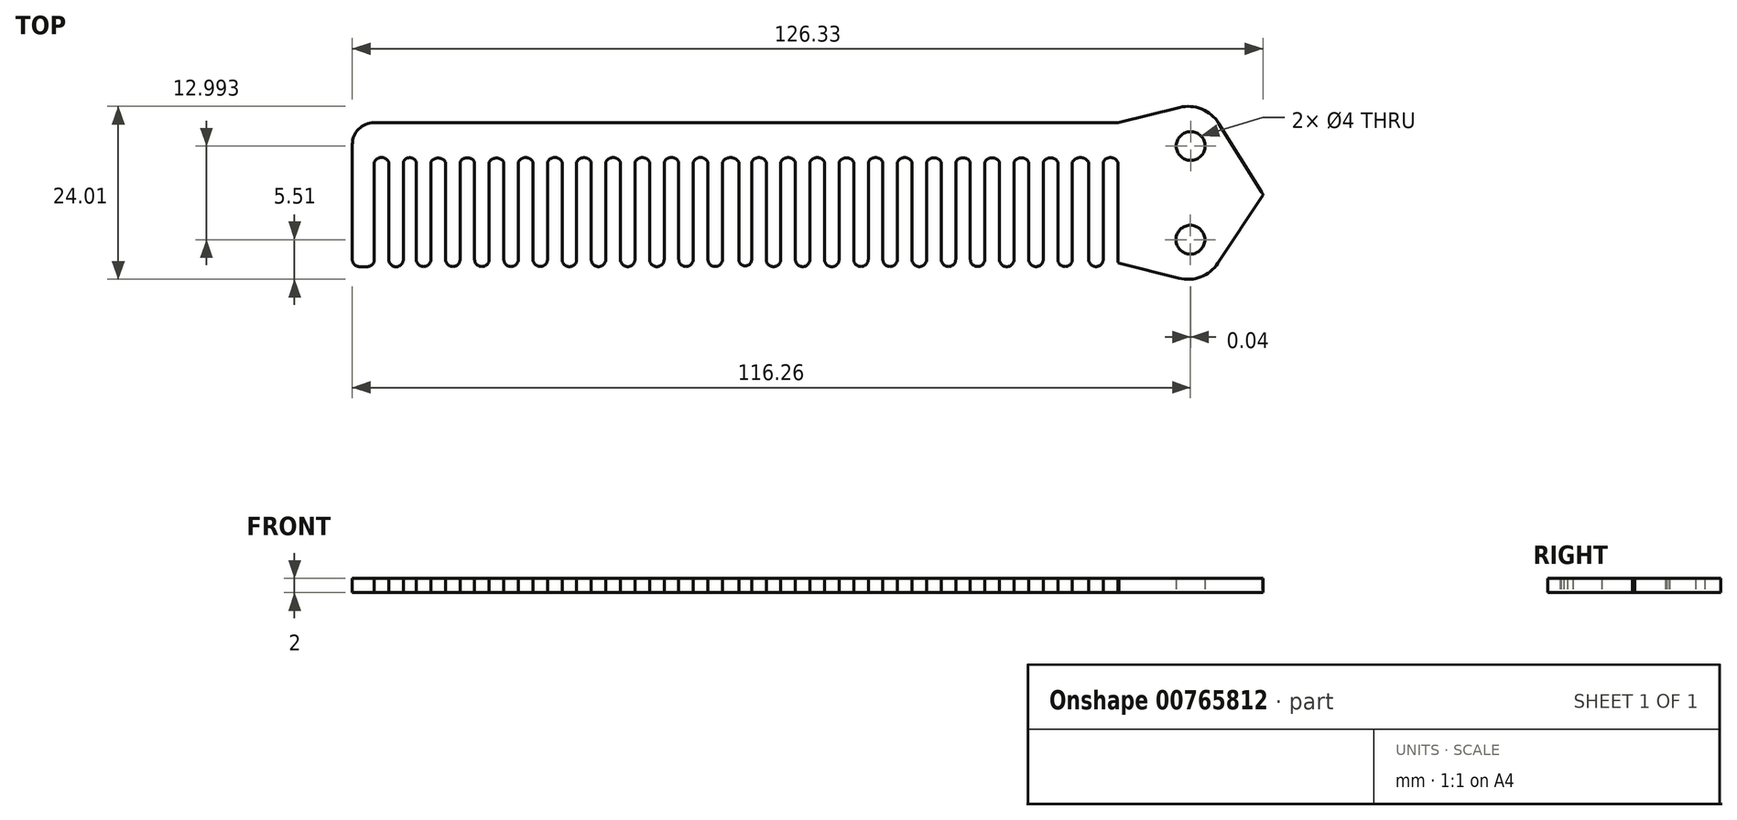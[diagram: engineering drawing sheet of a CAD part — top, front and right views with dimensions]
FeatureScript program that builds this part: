
annotation { "Feature Type Name" : "Feature", "Feature Type Description" : "" }
export const myFeature = defineFeature(function(context is Context, id is Id, definition is map)
    precondition{}
    {
        {
            var Q0;
            Q0=qCreatedBy(makeId("Top.planeOp"),FACE);
            var sketch = newSketch(context, id + "F0", { "sketchPlane" : qUnion([Q0])});
            skLineSegment(sketch, "E0.top", {"start": v(-46.52, -4.05) * mm, "end": v(-45.49, -4.05) * mm});
            skLineSegment(sketch, "E1", {"start": v(56.63, 10.5) * mm, "end": v(56.63, -3.03) * mm});
            skLineSegment(sketch, "E2", {"start": v(-44.48, 10.5) * mm, "end": v(-44.48, -3.03) * mm});
            skLineSegment(sketch, "E3", {"start": v(-47.53, 12.92) * mm, "end": v(-47.53, -3.03) * mm});
            skArc(sketch, "E4.filletArc", {"start": v(-44.5, 15.95) * mm, "mid": v(-46.64, 15.07) * mm, "end": v(-47.53, 12.92) * mm});
            skArc(sketch, "E5.filletArc", {"start": v(-47.53, -3.03) * mm, "mid": v(-47.24, -3.75) * mm, "end": v(-46.52, -4.05) * mm});
            skLineSegment(sketch, "E6", {"start": v(-42.48, 10.5) * mm, "end": v(-42.48, -3.04) * mm});
            skLineSegment(sketch, "E7", {"start": v(-40.45, 2.37) * mm, "end": v(-40.45, 10.5) * mm});
            skLineSegment(sketch, "E8", {"start": v(-40.45, 10.5) * mm, "end": v(-40.45, -3.04) * mm});
            skLineSegment(sketch, "E9", {"start": v(-38.66, 2.37) * mm, "end": v(-38.66, 10.5) * mm});
            skLineSegment(sketch, "E10", {"start": v(-38.66, 10.5) * mm, "end": v(-38.66, -3.03) * mm});
            skLineSegment(sketch, "E11", {"start": v(-36.63, 2.37) * mm, "end": v(-36.63, 10.5) * mm});
            skLineSegment(sketch, "E12", {"start": v(-36.63, 10.5) * mm, "end": v(-36.63, -3.03) * mm});
            skLineSegment(sketch, "E13", {"start": v(-34.61, 2.37) * mm, "end": v(-34.61, -3.03) * mm});
            skLineSegment(sketch, "E14", {"start": v(-34.61, -3.03) * mm, "end": v(-34.61, 10.5) * mm});
            skLineSegment(sketch, "E15", {"start": v(-32.59, 2.37) * mm, "end": v(-32.59, -3.03) * mm});
            skLineSegment(sketch, "E16", {"start": v(-32.59, -3.03) * mm, "end": v(-32.59, 10.5) * mm});
            skLineSegment(sketch, "E17", {"start": v(-30.57, 2.37) * mm, "end": v(-30.57, -3.03) * mm});
            skLineSegment(sketch, "E18", {"start": v(-30.57, -3.03) * mm, "end": v(-30.57, 10.5) * mm});
            skLineSegment(sketch, "E19", {"start": v(-28.54, 2.37) * mm, "end": v(-28.54, 10.5) * mm});
            skLineSegment(sketch, "E20", {"start": v(-28.54, 10.5) * mm, "end": v(-28.54, -3.03) * mm});
            skLineSegment(sketch, "E21", {"start": v(-26.52, 2.37) * mm, "end": v(-26.52, 10.5) * mm});
            skLineSegment(sketch, "E22", {"start": v(-26.52, 10.5) * mm, "end": v(-26.52, -3.03) * mm});
            skLineSegment(sketch, "E23", {"start": v(-24.5, 2.37) * mm, "end": v(-24.5, 10.5) * mm});
            skLineSegment(sketch, "E24", {"start": v(-24.5, 10.5) * mm, "end": v(-24.5, -3.03) * mm});
            skLineSegment(sketch, "E25", {"start": v(-22.48, 2.37) * mm, "end": v(-22.48, 10.5) * mm});
            skLineSegment(sketch, "E26", {"start": v(-22.48, 10.5) * mm, "end": v(-22.48, -3.03) * mm});
            skLineSegment(sketch, "E27", {"start": v(-20.45, 2.37) * mm, "end": v(-20.45, -3.03) * mm});
            skLineSegment(sketch, "E28", {"start": v(-20.45, -3.03) * mm, "end": v(-20.45, 10.5) * mm});
            skLineSegment(sketch, "E29", {"start": v(-18.43, 2.37) * mm, "end": v(-18.43, 10.5) * mm});
            skLineSegment(sketch, "E30", {"start": v(-18.43, 10.5) * mm, "end": v(-18.43, -3.03) * mm});
            skLineSegment(sketch, "E31", {"start": v(-16.4, 2.37) * mm, "end": v(-16.4, -3.03) * mm});
            skLineSegment(sketch, "E32", {"start": v(-16.4, -3.03) * mm, "end": v(-16.4, 10.5) * mm});
            skLineSegment(sketch, "E33", {"start": v(-14.39, 2.37) * mm, "end": v(-14.39, -3.03) * mm});
            skLineSegment(sketch, "E34", {"start": v(-14.39, -3.03) * mm, "end": v(-14.39, 10.5) * mm});
            skLineSegment(sketch, "E35", {"start": v(-12.36, 2.37) * mm, "end": v(-12.36, 10.5) * mm});
            skLineSegment(sketch, "E36", {"start": v(-12.36, 10.5) * mm, "end": v(-12.36, -3.03) * mm});
            skLineSegment(sketch, "E37", {"start": v(-10.34, 2.37) * mm, "end": v(-10.34, 10.5) * mm});
            skLineSegment(sketch, "E38", {"start": v(-10.34, 10.5) * mm, "end": v(-10.34, -3.03) * mm});
            skLineSegment(sketch, "E39", {"start": v(-8.32, 2.37) * mm, "end": v(-8.32, -3.03) * mm});
            skLineSegment(sketch, "E40", {"start": v(-8.32, -3.03) * mm, "end": v(-8.32, 10.5) * mm});
            skLineSegment(sketch, "E41", {"start": v(-6.3, 2.37) * mm, "end": v(-6.3, 10.5) * mm});
            skLineSegment(sketch, "E42", {"start": v(-6.3, 10.5) * mm, "end": v(-6.3, -3.03) * mm});
            skLineSegment(sketch, "E43", {"start": v(-4.27, 2.37) * mm, "end": v(-4.27, 10.5) * mm});
            skLineSegment(sketch, "E44", {"start": v(-4.27, 10.5) * mm, "end": v(-4.27, -3.03) * mm});
            skLineSegment(sketch, "E45", {"start": v(-2.25, 2.37) * mm, "end": v(-2.25, 10.5) * mm});
            skLineSegment(sketch, "E46", {"start": v(-2.25, 10.5) * mm, "end": v(-2.25, -3.03) * mm});
            skLineSegment(sketch, "E47", {"start": v(-0.23, 2.37) * mm, "end": v(-0.23, -3.03) * mm});
            skLineSegment(sketch, "E48", {"start": v(-0.23, -3.03) * mm, "end": v(-0.23, 10.5) * mm});
            skLineSegment(sketch, "E49", {"start": v(1.8, 2.37) * mm, "end": v(1.8, 10.5) * mm});
            skLineSegment(sketch, "E50", {"start": v(1.8, 10.5) * mm, "end": v(1.8, -3.03) * mm});
            skLineSegment(sketch, "E51", {"start": v(3.82, 2.37) * mm, "end": v(3.82, -3.03) * mm});
            skLineSegment(sketch, "E52", {"start": v(3.82, -3.03) * mm, "end": v(3.82, 10.5) * mm});
            skLineSegment(sketch, "E53", {"start": v(6.08, 2.37) * mm, "end": v(6.08, 10.5) * mm});
            skLineSegment(sketch, "E54", {"start": v(6.08, 10.5) * mm, "end": v(6.08, -3.03) * mm});
            skLineSegment(sketch, "E55", {"start": v(7.86, 2.37) * mm, "end": v(7.86, 10.5) * mm});
            skLineSegment(sketch, "E56", {"start": v(7.86, 10.5) * mm, "end": v(7.86, -3.03) * mm});
            skLineSegment(sketch, "E57", {"start": v(9.89, 2.37) * mm, "end": v(9.89, 10.5) * mm});
            skLineSegment(sketch, "E58", {"start": v(9.89, 10.5) * mm, "end": v(9.89, -3.03) * mm});
            skLineSegment(sketch, "E59", {"start": v(11.9, 2.37) * mm, "end": v(11.9, 10.5) * mm});
            skLineSegment(sketch, "E60", {"start": v(11.9, 10.5) * mm, "end": v(11.9, -3.03) * mm});
            skLineSegment(sketch, "E61", {"start": v(13.93, 2.37) * mm, "end": v(13.93, 10.5) * mm});
            skLineSegment(sketch, "E62", {"start": v(13.93, 10.5) * mm, "end": v(13.93, -3.03) * mm});
            skLineSegment(sketch, "E63", {"start": v(15.95, 2.37) * mm, "end": v(15.95, 10.5) * mm});
            skLineSegment(sketch, "E64", {"start": v(15.95, 10.5) * mm, "end": v(15.95, -3.03) * mm});
            skLineSegment(sketch, "E65", {"start": v(17.98, 10.5) * mm, "end": v(17.98, -3.06) * mm});
            skLineSegment(sketch, "E66", {"start": v(20, 2.37) * mm, "end": v(20, 10.5) * mm});
            skLineSegment(sketch, "E67", {"start": v(20, 10.5) * mm, "end": v(20, -3.06) * mm});
            skLineSegment(sketch, "E68", {"start": v(22.02, 2.37) * mm, "end": v(22.02, 10.5) * mm});
            skLineSegment(sketch, "E69", {"start": v(24.04, 2.37) * mm, "end": v(24.04, 10.5) * mm});
            skLineSegment(sketch, "E70", {"start": v(24.04, 2.37) * mm, "end": v(24.04, -3.03) * mm});
            skLineSegment(sketch, "E71", {"start": v(26.07, 2.37) * mm, "end": v(26.07, 10.5) * mm});
            skLineSegment(sketch, "E72", {"start": v(26.07, 10.5) * mm, "end": v(26.07, -3.03) * mm});
            skLineSegment(sketch, "E73", {"start": v(28.09, 2.37) * mm, "end": v(28.09, 10.5) * mm});
            skLineSegment(sketch, "E74", {"start": v(28.09, 2.37) * mm, "end": v(28.09, -3.03) * mm});
            skLineSegment(sketch, "E75", {"start": v(30.11, 2.37) * mm, "end": v(30.11, 10.5) * mm});
            skLineSegment(sketch, "E76", {"start": v(30.11, 10.5) * mm, "end": v(30.11, -3.03) * mm});
            skLineSegment(sketch, "E77", {"start": v(32.13, 2.37) * mm, "end": v(32.13, 10.5) * mm});
            skLineSegment(sketch, "E78", {"start": v(32.13, 10.5) * mm, "end": v(32.13, -3.03) * mm});
            skLineSegment(sketch, "E79", {"start": v(34.16, 2.37) * mm, "end": v(34.16, 10.5) * mm});
            skLineSegment(sketch, "E80", {"start": v(34.16, 10.5) * mm, "end": v(34.16, -3.03) * mm});
            skLineSegment(sketch, "E81", {"start": v(36.18, 2.37) * mm, "end": v(36.18, 10.5) * mm});
            skLineSegment(sketch, "E82", {"start": v(36.18, 10.5) * mm, "end": v(36.18, -3.03) * mm});
            skLineSegment(sketch, "E83", {"start": v(38.2, 2.37) * mm, "end": v(38.2, 10.5) * mm});
            skLineSegment(sketch, "E84", {"start": v(38.2, 10.5) * mm, "end": v(38.2, -3.03) * mm});
            skLineSegment(sketch, "E85", {"start": v(40.23, 2.37) * mm, "end": v(40.23, 10.5) * mm});
            skLineSegment(sketch, "E86", {"start": v(40.23, 10.5) * mm, "end": v(40.23, -3.03) * mm});
            skLineSegment(sketch, "E87", {"start": v(42.25, 2.37) * mm, "end": v(42.25, 10.5) * mm});
            skLineSegment(sketch, "E88", {"start": v(42.25, 10.5) * mm, "end": v(42.25, -3.03) * mm});
            skLineSegment(sketch, "E89", {"start": v(44.27, 2.37) * mm, "end": v(44.27, 10.5) * mm});
            skLineSegment(sketch, "E90", {"start": v(44.27, 10.5) * mm, "end": v(44.27, -3.03) * mm});
            skLineSegment(sketch, "E91", {"start": v(46.3, 2.37) * mm, "end": v(46.3, 10.5) * mm});
            skLineSegment(sketch, "E92", {"start": v(46.3, 10.5) * mm, "end": v(46.3, -3.03) * mm});
            skLineSegment(sketch, "E93", {"start": v(48.32, 2.37) * mm, "end": v(48.32, 10.5) * mm});
            skLineSegment(sketch, "E94", {"start": v(48.32, 10.5) * mm, "end": v(48.32, -3.03) * mm});
            skLineSegment(sketch, "E95", {"start": v(50.34, 2.37) * mm, "end": v(50.34, 10.5) * mm});
            skLineSegment(sketch, "E96", {"start": v(50.34, 10.5) * mm, "end": v(50.34, -3.03) * mm});
            skLineSegment(sketch, "E97", {"start": v(52.36, 2.37) * mm, "end": v(52.36, 10.5) * mm});
            skLineSegment(sketch, "E98", {"start": v(52.36, 10.5) * mm, "end": v(52.36, -3.03) * mm});
            skLineSegment(sketch, "E99", {"start": v(54.6, 2.37) * mm, "end": v(54.6, 10.5) * mm});
            skLineSegment(sketch, "E100", {"start": v(54.6, 10.5) * mm, "end": v(54.6, -3.03) * mm});
            skLineSegment(sketch, "E101", {"start": v(58.65, 10.5) * mm, "end": v(58.65, -3.18) * mm});
            skArc(sketch, "E102.filletArc", {"start": v(-45.49, -4.05) * mm, "mid": v(-44.77, -3.75) * mm, "end": v(-44.48, -3.03) * mm});
            skArc(sketch, "E103", {"start": v(-42.48, -3.03) * mm, "mid": v(-41.46, -4.05) * mm, "end": v(-40.45, -3.03) * mm});
            skArc(sketch, "E104", {"start": v(-38.66, -3.03) * mm, "mid": v(-37.65, -4.03) * mm, "end": v(-36.63, -3.03) * mm});
            skArc(sketch, "E105", {"start": v(-34.61, -3.03) * mm, "mid": v(-33.6, -4.03) * mm, "end": v(-32.59, -3.03) * mm});
            skArc(sketch, "E106", {"start": v(-30.57, -3.03) * mm, "mid": v(-29.55, -4.03) * mm, "end": v(-28.54, -3.03) * mm});
            skArc(sketch, "E107", {"start": v(-26.52, -3.03) * mm, "mid": v(-25.5, -4.03) * mm, "end": v(-24.5, -3.03) * mm});
            skArc(sketch, "E108", {"start": v(-22.48, -3.03) * mm, "mid": v(-21.46, -4.02) * mm, "end": v(-20.45, -3.03) * mm});
            skArc(sketch, "E109", {"start": v(-18.43, -3.03) * mm, "mid": v(-17.42, -4.05) * mm, "end": v(-16.4, -3.03) * mm});
            skArc(sketch, "E110", {"start": v(-14.39, -3.03) * mm, "mid": v(-13.37, -4.03) * mm, "end": v(-12.36, -3.03) * mm});
            skArc(sketch, "E111", {"start": v(-10.34, -3.03) * mm, "mid": v(-9.33, -4.03) * mm, "end": v(-8.32, -3.03) * mm});
            skArc(sketch, "E112", {"start": v(-6.3, -3.03) * mm, "mid": v(-5.28, -4.03) * mm, "end": v(-4.27, -3.03) * mm});
            skArc(sketch, "E113", {"start": v(-2.25, -3.03) * mm, "mid": v(-1.24, -4.03) * mm, "end": v(-0.23, -3.03) * mm});
            skArc(sketch, "E114", {"start": v(1.8, -3.03) * mm, "mid": v(2.8, -4.02) * mm, "end": v(3.82, -3.03) * mm});
            skArc(sketch, "E115", {"start": v(9.89, -3.03) * mm, "mid": v(10.9, -4.05) * mm, "end": v(11.9, -3.03) * mm});
            skArc(sketch, "E116", {"start": v(13.93, -3.03) * mm, "mid": v(14.94, -4.05) * mm, "end": v(15.95, -3.03) * mm});
            skArc(sketch, "E117", {"start": v(17.98, -3.03) * mm, "mid": v(18.99, -4.06) * mm, "end": v(20, -3.03) * mm});
            skArc(sketch, "E118", {"start": v(22.02, -3.03) * mm, "mid": v(23.03, -4.03) * mm, "end": v(24.04, -3.03) * mm});
            skArc(sketch, "E119", {"start": v(26.07, -3.03) * mm, "mid": v(27.08, -4.03) * mm, "end": v(28.09, -3.03) * mm});
            skArc(sketch, "E120", {"start": v(30.11, -3.03) * mm, "mid": v(31.12, -4.04) * mm, "end": v(32.13, -3.03) * mm});
            skArc(sketch, "E121", {"start": v(34.16, -3.03) * mm, "mid": v(35.17, -4.03) * mm, "end": v(36.18, -3.03) * mm});
            skArc(sketch, "E122", {"start": v(38.2, -3.03) * mm, "mid": v(39.21, -4.02) * mm, "end": v(40.23, -3.03) * mm});
            skArc(sketch, "E123", {"start": v(42.25, -3.03) * mm, "mid": v(43.26, -4.05) * mm, "end": v(44.27, -3.03) * mm});
            skArc(sketch, "E124", {"start": v(46.3, -3.03) * mm, "mid": v(47.3, -4.04) * mm, "end": v(48.32, -3.03) * mm});
            skArc(sketch, "E125", {"start": v(50.34, -3.03) * mm, "mid": v(51.35, -4.03) * mm, "end": v(52.36, -3.03) * mm});
            skArc(sketch, "E126", {"start": v(54.6, -3.03) * mm, "mid": v(55.62, -4.04) * mm, "end": v(56.63, -3.03) * mm});
            skArc(sketch, "E127.filletArc", {"start": v(58.65, -3.18) * mm, "mid": v(58.7, -3.38) * mm, "end": v(58.81, -3.55) * mm});
            skArc(sketch, "E128", {"start": v(6.08, -3.03) * mm, "mid": v(6.97, -3.93) * mm, "end": v(7.86, -3.03) * mm});
            skArc(sketch, "E129", {"start": v(-42.48, 10.5) * mm, "mid": v(-43.48, 11.12) * mm, "end": v(-44.48, 10.5) * mm});
            skArc(sketch, "E130", {"start": v(-38.66, 10.5) * mm, "mid": v(-39.55, 11.1) * mm, "end": v(-40.45, 10.5) * mm});
            skArc(sketch, "E131", {"start": v(-34.61, 10.5) * mm, "mid": v(-35.62, 11.04) * mm, "end": v(-36.63, 10.5) * mm});
            skArc(sketch, "E132", {"start": v(-30.57, 10.5) * mm, "mid": v(-31.58, 11.08) * mm, "end": v(-32.59, 10.5) * mm});
            skArc(sketch, "E133", {"start": v(-26.52, 10.5) * mm, "mid": v(-27.53, 11.04) * mm, "end": v(-28.54, 10.5) * mm});
            skArc(sketch, "E134", {"start": v(-22.48, 10.5) * mm, "mid": v(-23.49, 11.1) * mm, "end": v(-24.5, 10.5) * mm});
            skArc(sketch, "E135", {"start": v(-14.39, 10.5) * mm, "mid": v(-15.4, 11.1) * mm, "end": v(-16.4, 10.5) * mm});
            skArc(sketch, "E136", {"start": v(-18.43, 10.5) * mm, "mid": v(-19.44, 11.11) * mm, "end": v(-20.45, 10.5) * mm});
            skArc(sketch, "E137", {"start": v(-10.34, 10.5) * mm, "mid": v(-11.35, 11.1) * mm, "end": v(-12.36, 10.5) * mm});
            skArc(sketch, "E138", {"start": v(-6.3, 10.5) * mm, "mid": v(-7.3, 11.1) * mm, "end": v(-8.32, 10.5) * mm});
            skArc(sketch, "E139", {"start": v(-2.25, 10.5) * mm, "mid": v(-3.26, 11.12) * mm, "end": v(-4.27, 10.5) * mm});
            skArc(sketch, "E140", {"start": v(1.8, 10.5) * mm, "mid": v(0.78, 11.11) * mm, "end": v(-0.23, 10.5) * mm});
            skArc(sketch, "E141", {"start": v(6.08, 10.5) * mm, "mid": v(4.95, 11.1) * mm, "end": v(3.82, 10.5) * mm});
            skArc(sketch, "E142", {"start": v(9.89, 10.5) * mm, "mid": v(8.87, 11.1) * mm, "end": v(7.86, 10.5) * mm});
            skArc(sketch, "E143", {"start": v(13.93, 10.5) * mm, "mid": v(12.92, 11.1) * mm, "end": v(11.9, 10.5) * mm});
            skArc(sketch, "E144", {"start": v(17.98, 10.5) * mm, "mid": v(16.97, 11.1) * mm, "end": v(15.95, 10.5) * mm});
            skArc(sketch, "E145", {"start": v(22.02, 10.5) * mm, "mid": v(21.01, 11.06) * mm, "end": v(20, 10.5) * mm});
            skArc(sketch, "E146", {"start": v(26.07, 10.5) * mm, "mid": v(25.06, 11.1) * mm, "end": v(24.04, 10.5) * mm});
            skArc(sketch, "E147", {"start": v(30.11, 10.5) * mm, "mid": v(29.1, 11.1) * mm, "end": v(28.09, 10.5) * mm});
            skArc(sketch, "E148", {"start": v(34.16, 10.5) * mm, "mid": v(33.15, 11.08) * mm, "end": v(32.13, 10.5) * mm});
            skArc(sketch, "E149", {"start": v(38.2, 10.5) * mm, "mid": v(37.2, 11.08) * mm, "end": v(36.18, 10.5) * mm});
            skArc(sketch, "E150", {"start": v(42.25, 10.5) * mm, "mid": v(41.24, 11.08) * mm, "end": v(40.23, 10.5) * mm});
            skArc(sketch, "E151", {"start": v(46.3, 10.5) * mm, "mid": v(45.28, 11.08) * mm, "end": v(44.27, 10.5) * mm});
            skArc(sketch, "E152", {"start": v(50.34, 10.5) * mm, "mid": v(49.33, 11.08) * mm, "end": v(48.32, 10.5) * mm});
            skArc(sketch, "E153", {"start": v(54.6, 10.5) * mm, "mid": v(53.49, 11.1) * mm, "end": v(52.36, 10.5) * mm});
            skArc(sketch, "E154", {"start": v(58.65, 10.5) * mm, "mid": v(57.64, 11.1) * mm, "end": v(56.63, 10.5) * mm});
            skLineSegment(sketch, "E155", {"start": v(22.02, 2.37) * mm, "end": v(22.02, -3.03) * mm});
            skLineSegment(sketch, "E156", {"start": v(78.8, 5.95) * mm, "end": v(78.8, 5.95) * mm});
            skLineSegment(sketch, "E157", {"start": v(-44.5, 15.95) * mm, "end": v(58.65, 15.95) * mm});
            skPoint(sketch, "E158.visualSharp", {"position": v(78.8, -4.05) * mm});
            skPoint(sketch, "E159.visualSharp", {"position": v(78.8, 15.95) * mm});
            skPoint(sketch, "E160.visualSharp", {"position": v(78.8, 5.95) * mm});
            skCircle(sketch, "E161", {"center": v(68.73, -0.29) * mm, "radius": 2 * mm});
            skCircle(sketch, "E162", {"center": v(68.77, 12.7) * mm, "radius": 2 * mm});
            skLineSegment(sketch, "E163", {"start": v(72.54, -3.55) * mm, "end": v(78.8, 5.94) * mm});
            skLineSegment(sketch, "E164", {"start": v(72.66, 15.85) * mm, "end": v(78.6, 6.3) * mm});
            skLineSegment(sketch, "E165", {"start": v(58.65, 15.95) * mm, "end": v(67.22, 18.06) * mm});
            skLineSegment(sketch, "E166", {"start": v(58.81, -3.55) * mm, "end": v(67.14, -5.65) * mm});
            skPoint(sketch, "E167.visualSharp", {"position": v(70.75, 18.93) * mm});
            skArc(sketch, "E167.filletArc", {"start": v(72.66, 15.85) * mm, "mid": v(70.3, 17.84) * mm, "end": v(67.22, 18.06) * mm});
            skPoint(sketch, "E168.visualSharp", {"position": v(70.58, -6.52) * mm});
            skArc(sketch, "E168.filletArc", {"start": v(67.14, -5.65) * mm, "mid": v(70.17, -5.46) * mm, "end": v(72.54, -3.55) * mm});
            skArc(sketch, "E169", {"start": v(78.8, 5.94) * mm, "mid": v(78.72, 6.13) * mm, "end": v(78.6, 6.3) * mm});
            skSolve(sketch);
        }
        {
            var Q0;
            Q0=qSketchRegion(id+"F0",true);
            var Q1;
            Q1=makeQuery(id+"F0.imprint","IMPRINT",FACE,{"disambiguationData":[TD([[makeQuery(id+"F0.imprint","IMPRINT",EDGE,{"derivedFrom":sQuery(id+"F0.wireOp",EDGE,"1oXmgVZ5-gnLq-iHea-oESG-ihjMs6EF8sqd")}),1.0]])]});
            var Q2;
            Q2=makeQuery(id+"F0.imprint","IMPRINT",FACE,{"disambiguationData":[TD([[makeQuery(id+"F0.imprint","IMPRINT",EDGE,{"derivedFrom":sQuery(id+"F0.wireOp",EDGE,"hkDLLBfR-qxi3-HcG5-FM2N-qt6i9bJRYM3o")}),1.0]])]});
            extrude(context, id + "F1", {"entities" : qUnion([Q0, Q1, Q2]), "depth" : 2 * mm, "offsetDistance" : 25 * mm});
        }
    });
